# Revit family: LF-LED-414xxx
name_source: partatom
category: Leuchten
units: mm (PartAtom-declared; Revit-internal decimal feet)

## family parameters
Basisbauteil = Fläche
Beim Laden mit Abzugskörper schneiden = Nein
Bemaßung runder Anschluss = Durchmesser verwenden
Gemeinsam genutzt = Nein
Lichtquelle = Ja
OmniClass-Nummer = 23.80.70.11
OmniClass-Titel = Luminaries for Internal Lighting
Raumberechnungspunkt = Nein
Teiletyp = Normal

## types (8) — shared parameters
Baugruppenkennzeichen = D5020200
Datei für fotometrisches Netz = LF-LED 414.IES
Emissionsform beim Rendern sichtbar = Nein
Farbfilter = 16777215
Farbtemperaturverschiebung bei Dämpfen der Lampe = <Keine Auswahl>
Hersteller = RIDI Leuchten GmbH
Lampe = LED
Neigungswinkel = 90.00°
URL = www.ridi.de
Von Breite des Rechtecks ausssenden = 620 mm  [stored 2.03412 ft]
Von Länge des Rechtecks aussenden = 620 mm  [stored 2.03412 ft]
brand = RIDI
conformity mark = CE
electrical safety class = 1
height = 81 mm  [stored 0.265748 ft]
ingress protection (IP) code = IP64
length = 620 mm  [stored 2.03412 ft]
nominal frequency = 50-60Hz
nominal voltage = 230
voltage type (AC, DC, UC) = AC
weight = 8,16
width = 620 mm  [stored 2.03412 ft]
zero-valued in all types: Vorgabe-Ansicht

## per-type parameters (varying)
| type | Modell | Scheinlast | rated input power |
| LF-LED-414/10000/830 | 0422158//649 | 64 VA | 64 |
| LF-LED-414/10000/830-DALI | 0432158//649 | 64 VA | 64 |
| LF-LED-414/10400/840 | 0422158 | 64 VA | 64 |
| LF-LED-414/10400/840-DALI | 0432158 | 64 VA | 64 |
| LF-LED-414/5000/830 | 0422155//649 | 32 VA | 32 |
| LF-LED-414/5000/830-DALI | 0432155//649 | 32 VA | 32 |
| LF-LED-414/5200/840 | 0422155 | 32 VA | 32 |
| LF-LED-414/5200/840-DALI | 0432155 | 32 VA | 32 |

note: column(s) folded — value = type name in every type: product name

note: [stored X ft] marks values corroborated as IEEE doubles in the binary element streams (Revit-internal decimal feet)
